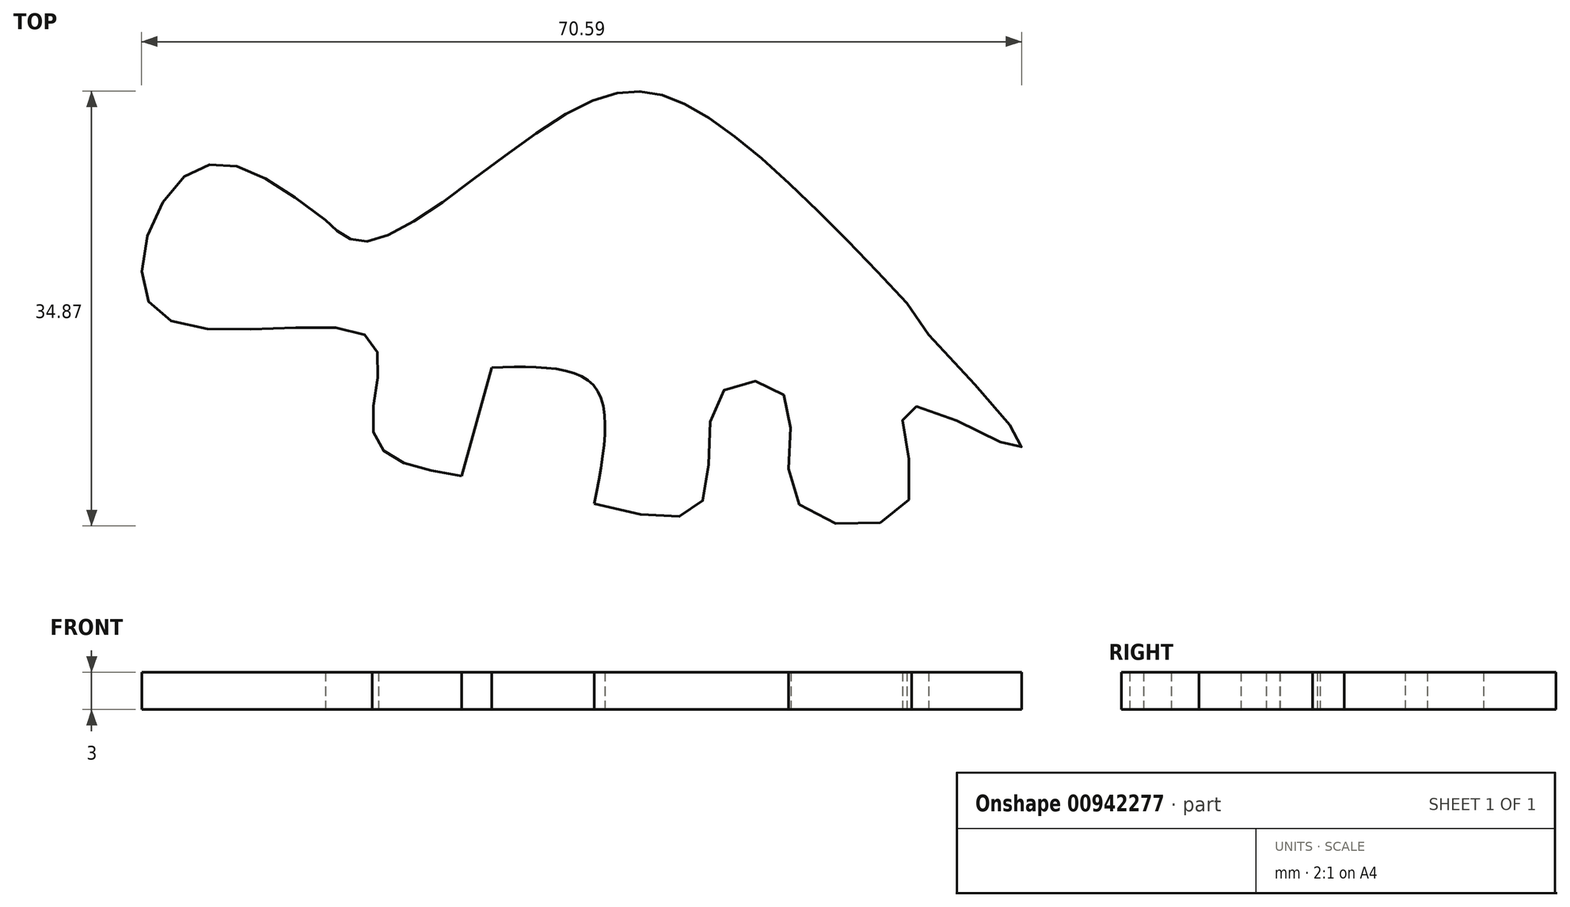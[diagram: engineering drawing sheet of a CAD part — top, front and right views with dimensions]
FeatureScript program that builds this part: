
annotation { "Feature Type Name" : "Feature", "Feature Type Description" : "" }
export const myFeature = defineFeature(function(context is Context, id is Id, definition is map)
    precondition{}
    {
        {
            var Q0;
            Q0=qCreatedBy(makeId("Top.planeOp"),FACE);
            var sketch = newSketch(context, id + "F0", { "sketchPlane" : qUnion([Q0])});
            skFitSpline(sketch, "E0", {"points": [v(-21.57, 3.89) * mm, v(-32.31, 7.78) * mm, v(-35.1, -3.52) * mm, v(-18.06, -5.56) * mm, v(-17.69, -13.33) * mm, v(-10.65, -16.67) * mm], "startDerivative": vector(-55.94, 42.53) * mm, "endDerivative": vector(57.13, -9.45) * mm});
            skFitSpline(sketch, "E1", {"points": [v(-10.65, -16.67) * mm, v(-8.24, -7.96) * mm], "startDerivative": vector(2.4, 8.7) * mm, "endDerivative": vector(2.4, 8.7) * mm});
            skFitSpline(sketch, "E2", {"points": [v(-8.24, -7.96) * mm, v(0, -9.44) * mm, v(0, -18.89) * mm], "startDerivative": vector(21.11, 0.65) * mm, "endDerivative": vector(-4.38, -22.27) * mm});
            skFitSpline(sketch, "E3", {"points": [v(-21.57, 3.89) * mm, v(-17.87, 2.22) * mm, v(-1.57, 12.78) * mm, v(7.69, 12.96) * mm, v(25.1, -2.78) * mm], "startDerivative": vector(21.04, -21.24) * mm, "endDerivative": vector(55.3, -58.11) * mm});
            skLineSegment(sketch, "E4.bottom", {"start": v(-38.98, 47.04) * mm, "end": v(41.02, 47.04) * mm});
            skLineSegment(sketch, "E4.top", {"start": v(-38.98, -32.96) * mm, "end": v(41.02, -32.96) * mm});
            skLineSegment(sketch, "E4.left", {"start": v(-38.98, 47.04) * mm, "end": v(-38.98, -32.96) * mm});
            skLineSegment(sketch, "E4.right", {"start": v(41.02, 47.04) * mm, "end": v(41.02, -32.96) * mm});
            skFitSpline(sketch, "E5", {"points": [v(0, -18.89) * mm, v(8.57, -18.89) * mm, v(10.09, -10.1) * mm, v(15.3, -10.31) * mm, v(16.39, -18.89) * mm, v(25.1, -18.89) * mm, v(25.1, -11.18) * mm, v(33.98, -14.44) * mm, v(26.81, -5.32) * mm], "startDerivative": vector(88.03, -22.6) * mm, "endDerivative": vector(-89.1, 95.02) * mm});
            skFitSpline(sketch, "E6", {"points": [v(25.1, -2.78) * mm, v(26.81, -5.32) * mm], "startDerivative": vector(1.72, -2.54) * mm, "endDerivative": vector(1.72, -2.54) * mm});
            skSolve(sketch);
        }
        {
            var Q0;
            Q0=makeQuery(id+"F0.imprint","IMPRINT",FACE,{"disambiguationData":[TD([[makeQuery(id+"F0.imprint","IMPRINT",EDGE,{"derivedFrom":sQuery(id+"F0.wireOp",EDGE,"E0")}),1.0]])]});
            extrude(context, id + "F1", {"entities" : qUnion([Q0]), "depth" : 3 * mm, "offsetDistance" : 25.4 * mm});
        }
    });
